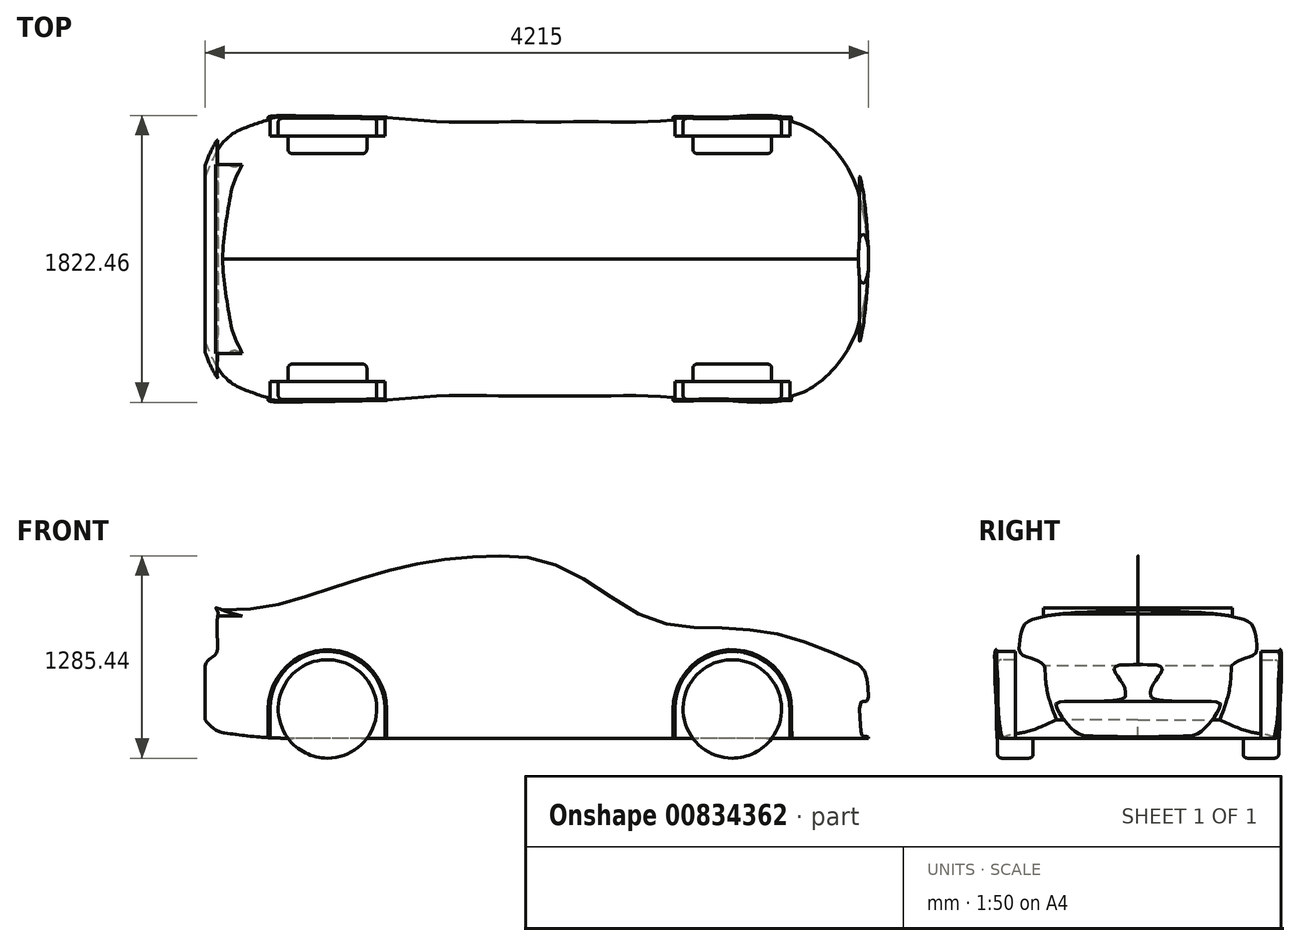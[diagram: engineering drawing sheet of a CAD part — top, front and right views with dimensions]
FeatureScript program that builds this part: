
annotation { "Feature Type Name" : "Feature", "Feature Type Description" : "" }
export const myFeature = defineFeature(function(context is Context, id is Id, definition is map)
    precondition{}
    {
        {
            var Q0;
            Q0=qCreatedBy(makeId("Right.planeOp"),FACE);
            cPlane(context, id + "F0", {"entities" : qUnion([Q0]), "cplaneType" : CPlaneType.OFFSET, "offset" : 400 * mm, "width" : 150 * mm, "height" : 150 * mm});
        }
        {
            var Q0;
            Q0=qCreatedBy(id+"F0.planeOp",FACE);
            cPlane(context, id + "F1", {"entities" : qUnion([Q0]), "cplaneType" : CPlaneType.OFFSET, "offset" : 250 * mm, "width" : 150 * mm, "height" : 150 * mm});
        }
        {
            var Q0;
            Q0=qCreatedBy(id+"F1.planeOp",FACE);
            cPlane(context, id + "F2", {"entities" : qUnion([Q0]), "cplaneType" : CPlaneType.OFFSET, "offset" : 470 * mm, "width" : 150 * mm, "height" : 150 * mm});
        }
        {
            var Q0;
            Q0=qCreatedBy(id+"F2.planeOp",FACE);
            cPlane(context, id + "F3", {"entities" : qUnion([Q0]), "cplaneType" : CPlaneType.OFFSET, "offset" : 390 * mm, "width" : 150 * mm, "height" : 150 * mm});
        }
        {
            var Q0;
            Q0=qCreatedBy(makeId("Right.planeOp"),FACE);
            cPlane(context, id + "F4", {"entities" : qUnion([Q0]), "cplaneType" : CPlaneType.OFFSET, "offset" : 650 * mm, "oppositeDirection" : true, "width" : 150 * mm, "height" : 150 * mm});
        }
        {
            var Q0;
            Q0=qCreatedBy(makeId("Right.planeOp"),FACE);
            cPlane(context, id + "F5", {"entities" : qUnion([Q0]), "cplaneType" : CPlaneType.OFFSET, "offset" : 1080 * mm, "oppositeDirection" : true, "width" : 150 * mm, "height" : 150 * mm});
        }
        {
            var Q0;
            Q0=qCreatedBy(id+"F5.planeOp",FACE);
            cPlane(context, id + "F6", {"entities" : qUnion([Q0]), "cplaneType" : CPlaneType.OFFSET, "offset" : 400 * mm, "oppositeDirection" : true, "width" : 150 * mm, "height" : 150 * mm});
        }
        {
            var Q0;
            Q0=qCreatedBy(id+"F6.planeOp",FACE);
            cPlane(context, id + "F7", {"entities" : qUnion([Q0]), "cplaneType" : CPlaneType.OFFSET, "offset" : 300 * mm, "oppositeDirection" : true, "width" : 150 * mm, "height" : 150 * mm});
        }
        {
            var Q0;
            Q0=qCreatedBy(makeId("Right.planeOp"),FACE);
            var sketch = newSketch(context, id + "F8", { "sketchPlane" : qUnion([Q0])});
            skLineSegment(sketch, "E0", {"start": v(0, 124.5) * mm, "end": v(870, 124.5) * mm});
            skFitSpline(sketch, "E1", {"points": [v(870, 124.5) * mm, v(891.11, 284.5) * mm, v(894.64, 458.04) * mm, v(887.8, 670.78) * mm, v(873.17, 769.8) * mm, v(845.6, 817.1) * mm, v(804.73, 858.33) * mm, v(772.04, 909.97) * mm, v(720.89, 1009.06) * mm, v(649.29, 1152.8) * mm, v(559.76, 1235.3) * mm, v(0, 1252.96) * mm], "startDerivative": vector(362.88, 1642) * mm, "endDerivative": vector(-2009.53, -25.16) * mm});
            skLineSegment(sketch, "E2", {"start": v(0, 0) * mm, "end": v(0, 1252.96) * mm});
            skSolve(sketch);
        }
        {
            var Q0;
            Q0=qCreatedBy(id+"F0.planeOp",FACE);
            var sketch = newSketch(context, id + "F9", { "sketchPlane" : qUnion([Q0])});
            skLineSegment(sketch, "E3", {"start": v(0, 124.5) * mm, "end": v(870, 124.5) * mm});
            skFitSpline(sketch, "E4", {"points": [v(870, 124.5) * mm, v(889.48, 284.5) * mm, v(893.13, 453.1) * mm, v(886.02, 666.74) * mm, v(878.45, 750.6) * mm, v(846.63, 809.81) * mm, v(806.15, 848.41) * mm, v(773.2, 873.84) * mm, v(733.56, 929.45) * mm, v(666.4, 987) * mm, v(525.26, 1024) * mm, v(0, 1039.03) * mm], "startDerivative": vector(258.1, 1763.42) * mm, "endDerivative": vector(-2429.32, 0) * mm});
            skLineSegment(sketch, "E5", {"start": v(0, 124.5) * mm, "end": v(0, 1039.03) * mm});
            skSolve(sketch);
        }
        {
            var Q0;
            Q0=qCreatedBy(id+"F1.planeOp",FACE);
            var sketch = newSketch(context, id + "F10", { "sketchPlane" : qUnion([Q0])});
            skLineSegment(sketch, "E6", {"start": v(0, 124.5) * mm, "end": v(870, 124.5) * mm});
            skFitSpline(sketch, "E7", {"points": [v(870, 124.5) * mm, v(892.1, 284.5) * mm, v(894.52, 460.26) * mm, v(887.06, 674.5) * mm, v(873.24, 753.16) * mm, v(845.97, 795) * mm, v(804.34, 823.62) * mm, v(744.49, 841.84) * mm, v(628.69, 860.05) * mm, v(503.78, 873.07) * mm, v(342.44, 883.47) * mm, v(0, 892.58) * mm], "startDerivative": vector(336.22, 2247.6) * mm, "endDerivative": vector(-2429.27, 12.93) * mm});
            skLineSegment(sketch, "E8", {"start": v(0, 124.5) * mm, "end": v(0, 892.58) * mm});
            skSolve(sketch);
        }
        {
            var Q0;
            Q0=qCreatedBy(id+"F4.planeOp",FACE);
            var sketch = newSketch(context, id + "F11", { "sketchPlane" : qUnion([Q0])});
            skLineSegment(sketch, "E9", {"start": v(0, 124.5) * mm, "end": v(870, 124.5) * mm});
            skFitSpline(sketch, "E10", {"points": [v(870, 124.5) * mm, v(891.22, 284.5) * mm, v(893.85, 457.43) * mm, v(888.43, 668) * mm, v(877.52, 766.78) * mm, v(847.35, 831) * mm, v(806.73, 867.36) * mm, v(772.55, 908.99) * mm, v(713.7, 1043.7) * mm, v(639.2, 1173.93) * mm, v(505.77, 1239) * mm, v(0, 1259.74) * mm], "startDerivative": vector(285.74, 2002.73) * mm, "endDerivative": vector(-2009.53, -25.16) * mm});
            skLineSegment(sketch, "E11", {"start": v(0, 0) * mm, "end": v(0, 1259.74) * mm});
            skSolve(sketch);
        }
        {
            var Q0;
            Q0=qCreatedBy(id+"F5.planeOp",FACE);
            var sketch = newSketch(context, id + "F12", { "sketchPlane" : qUnion([Q0])});
            skLineSegment(sketch, "E12", {"start": v(0, 124.5) * mm, "end": v(901.84, 124.5) * mm});
            skFitSpline(sketch, "E13", {"points": [v(901.84, 124.5) * mm, v(901.84, 445.34) * mm, v(897.17, 659.1) * mm, v(883.08, 776.07) * mm, v(850.9, 838.5) * mm, v(807.82, 870.25) * mm, v(762.15, 901.06) * mm, v(705.47, 979.53) * mm, v(608.15, 1094.45) * mm, v(391.22, 1147.4) * mm, v(0, 1167.07) * mm], "startDerivative": vector(56.05, 2605.66) * mm, "endDerivative": vector(-2009.53, -25.16) * mm});
            skLineSegment(sketch, "E14", {"start": v(0, 0) * mm, "end": v(0, 1167.07) * mm});
            skSolve(sketch);
        }
        {
            var Q0;
            Q0=qCreatedBy(id+"F6.planeOp",FACE);
            var sketch = newSketch(context, id + "F13", { "sketchPlane" : qUnion([Q0])});
            skLineSegment(sketch, "E15", {"start": v(0, 124.5) * mm, "end": v(905.35, 124.5) * mm});
            skFitSpline(sketch, "E16", {"points": [v(905.35, 124.5) * mm, v(911.49, 507.78) * mm, v(901.23, 717.66) * mm, v(864.15, 828.08) * mm, v(805.53, 864.3) * mm, v(709.87, 894.97) * mm, v(662.3, 933.8) * mm, v(611.81, 968.75) * mm, v(468.12, 1007.59) * mm, v(200.58, 1032.29) * mm, v(0, 1036.7) * mm], "startDerivative": vector(35.6, 1166.72) * mm, "endDerivative": vector(-2009.53, -25.16) * mm});
            skLineSegment(sketch, "E17", {"start": v(0, 100.04) * mm, "end": v(0, 1036.7) * mm});
            skSolve(sketch);
        }
        {
            var Q0;
            Q0=qCreatedBy(id+"F2.planeOp",FACE);
            var sketch = newSketch(context, id + "F14", { "sketchPlane" : qUnion([Q0])});
            skLineSegment(sketch, "E18", {"start": v(0, 124.5) * mm, "end": v(903.74, 124.5) * mm});
            skFitSpline(sketch, "E19", {"points": [v(903.74, 124.5) * mm, v(916.37, 455.49) * mm, v(900.5, 679.08) * mm, v(857.9, 771.6) * mm, v(782.93, 814.08) * mm, v(692.41, 799.23) * mm, v(637.01, 783.4) * mm, v(575.02, 780.76) * mm, v(449.7, 795.27) * mm, v(267.68, 816.38) * mm, v(0, 826.93) * mm], "startDerivative": vector(154.78, 2385.54) * mm, "endDerivative": vector(-2429.32, -1.4) * mm});
            skLineSegment(sketch, "E20", {"start": v(0, 124.5) * mm, "end": v(0, 826.93) * mm});
            skSolve(sketch);
        }
        {
            var Q0;
            Q0=qCreatedBy(id+"F3.planeOp",FACE);
            var sketch = newSketch(context, id + "F15", { "sketchPlane" : qUnion([Q0])});
            skLineSegment(sketch, "E21", {"start": v(0, 124.5) * mm, "end": v(885.85, 124.5) * mm});
            skFitSpline(sketch, "E22", {"points": [v(885.85, 124.5) * mm, v(903.62, 270.39) * mm, v(904.2, 467.45) * mm, v(859.81, 719.76) * mm, v(768.6, 771) * mm, v(666.13, 754.75) * mm, v(542.72, 724.7) * mm, v(464.05, 723.61) * mm, v(376.77, 736.54) * mm, v(261.46, 760.25) * mm, v(152.62, 774.26) * mm, v(0, 781.8) * mm], "startDerivative": vector(300.47, 1117.8) * mm, "endDerivative": vector(-2429.32, -1.4) * mm});
            skLineSegment(sketch, "E23", {"start": v(0, 124.5) * mm, "end": v(0, 781.8) * mm});
            skSolve(sketch);
        }
        {
            var Q0;
            Q0=qCreatedBy(id+"F3.planeOp",FACE);
            cPlane(context, id + "F16", {"entities" : qUnion([Q0]), "cplaneType" : CPlaneType.OFFSET, "offset" : 300 * mm, "width" : 150 * mm, "height" : 150 * mm});
        }
        {
            var Q0;
            Q0=qCreatedBy(id+"F16.planeOp",FACE);
            var sketch = newSketch(context, id + "F17", { "sketchPlane" : qUnion([Q0])});
            skLineSegment(sketch, "E24", {"start": v(0, 124.5) * mm, "end": v(728.16, 124.5) * mm});
            skFitSpline(sketch, "E25", {"points": [v(728.16, 124.5) * mm, v(790.88, 438.77) * mm, v(756.31, 575.08) * mm, v(668.27, 639.2) * mm, v(496.33, 652.7) * mm, v(405.95, 657.45) * mm, v(317.95, 663.4) * mm, v(215.67, 669.34) * mm, v(121.8, 673) * mm, v(0, 677.25) * mm], "startDerivative": vector(683.35, 2007.11) * mm, "endDerivative": vector(-1315.52, 16.5) * mm});
            skLineSegment(sketch, "E26", {"start": v(0, 124.5) * mm, "end": v(0, 677.25) * mm});
            skSolve(sketch);
        }
        {
            var Q0;
            Q0=qCreatedBy(id+"F16.planeOp",FACE);
            cPlane(context, id + "F18", {"entities" : qUnion([Q0]), "cplaneType" : CPlaneType.OFFSET, "offset" : 175 * mm, "width" : 150 * mm, "height" : 150 * mm});
        }
        {
            var Q0;
            Q0=qCreatedBy(id+"F18.planeOp",FACE);
            var sketch = newSketch(context, id + "F19", { "sketchPlane" : qUnion([Q0])});
            skLineSegment(sketch, "E27", {"start": v(0, 124.5) * mm, "end": v(450, 124.5) * mm});
            skFitSpline(sketch, "E28", {"points": [v(450, 124.5) * mm, v(487.77, 181.4) * mm, v(571.26, 329.58) * mm, v(600.39, 467.6) * mm, v(581.4, 527.1) * mm, v(497.82, 563.83) * mm, v(383.86, 580.3) * mm, v(269.9, 592.95) * mm, v(152.4, 598.78) * mm, v(0, 600) * mm], "startDerivative": vector(794.98, 1097.59) * mm, "endDerivative": vector(-2440.18, 24.53) * mm});
            skLineSegment(sketch, "E29", {"start": v(0, 124.5) * mm, "end": v(0, 600) * mm});
            skSolve(sketch);
        }
        {
            var Q0;
            Q0=qCreatedBy(id+"F18.planeOp",FACE);
            cPlane(context, id + "F20", {"entities" : qUnion([Q0]), "cplaneType" : CPlaneType.OFFSET, "offset" : 75 * mm, "width" : 150 * mm, "height" : 150 * mm});
        }
        {
            var Q0;
            Q0=qCreatedBy(id+"F20.planeOp",FACE);
            var sketch = newSketch(context, id + "F21", { "sketchPlane" : qUnion([Q0])});
            skLineSegment(sketch, "E30", {"start": v(0, 124.5) * mm, "end": v(20.31, 124.5) * mm});
            skFitSpline(sketch, "E31", {"points": [v(20.31, 124.5) * mm, v(48.12, 155) * mm, v(57.63, 231.82) * mm, v(57.08, 273.61) * mm, v(38.48, 458.21) * mm, v(16.04, 541.01) * mm, v(0, 565.46) * mm], "startDerivative": vector(421.48, 102.59) * mm, "endDerivative": vector(-203.78, 250.22) * mm});
            skLineSegment(sketch, "E32", {"start": v(0, 124.5) * mm, "end": v(0, 565.46) * mm});
            skSolve(sketch);
        }
        {
            var Q0;
            Q0=qCreatedBy(id+"F7.planeOp",FACE);
            var sketch = newSketch(context, id + "F22", { "sketchPlane" : qUnion([Q0])});
            skLineSegment(sketch, "E33", {"start": v(0, 131.73) * mm, "end": v(875, 131.73) * mm});
            skFitSpline(sketch, "E34", {"points": [v(875, 131.73) * mm, v(895.55, 627.68) * mm, v(848.53, 820.84) * mm, v(812.95, 851.34) * mm, v(754.12, 880.67) * mm, v(696.63, 896.7) * mm, v(604.5, 918.2) * mm, v(498.32, 932.44) * mm, v(350.54, 945.58) * mm, v(198.38, 953.24) * mm, v(0, 958.71) * mm], "startDerivative": vector(247.43, 1101.88) * mm, "endDerivative": vector(-2009.53, -25.16) * mm});
            skLineSegment(sketch, "E35", {"start": v(0, 131.73) * mm, "end": v(0, 958.71) * mm});
            skSolve(sketch);
        }
        {
            var Q0;
            Q0=qCreatedBy(id+"F7.planeOp",FACE);
            cPlane(context, id + "F23", {"entities" : qUnion([Q0]), "cplaneType" : CPlaneType.OFFSET, "offset" : 100 * mm, "oppositeDirection" : true, "width" : 150 * mm, "height" : 150 * mm});
        }
        {
            var Q0;
            Q0=qCreatedBy(id+"F23.planeOp",FACE);
            var sketch = newSketch(context, id + "F24", { "sketchPlane" : qUnion([Q0])});
            skLineSegment(sketch, "E36", {"start": v(0, 140.57) * mm, "end": v(840.25, 140.57) * mm});
            skFitSpline(sketch, "E37", {"points": [v(840.25, 140.57) * mm, v(875.51, 631.89) * mm, v(816.68, 820.6) * mm, v(761.84, 865.46) * mm, v(730.93, 879.42) * mm, v(659.57, 898.6) * mm, v(504.06, 921.3) * mm, v(347.08, 933.67) * mm, v(195.8, 942.23) * mm, v(0, 947.94) * mm], "startDerivative": vector(247.43, 1101.88) * mm, "endDerivative": vector(-2009.53, -25.16) * mm});
            skLineSegment(sketch, "E38", {"start": v(0, 140.57) * mm, "end": v(0, 947.94) * mm});
            skSolve(sketch);
        }
        {
            var Q0;
            Q0=qCreatedBy(id+"F23.planeOp",FACE);
            cPlane(context, id + "F25", {"entities" : qUnion([Q0]), "cplaneType" : CPlaneType.OFFSET, "offset" : 100 * mm, "oppositeDirection" : true, "width" : 150 * mm, "height" : 150 * mm});
        }
        {
            var Q0;
            Q0=qCreatedBy(id+"F25.planeOp",FACE);
            var sketch = newSketch(context, id + "F26", { "sketchPlane" : qUnion([Q0])});
            skLineSegment(sketch, "E39", {"start": v(0, 153.5) * mm, "end": v(793.13, 153.5) * mm});
            skFitSpline(sketch, "E40", {"points": [v(793.13, 153.5) * mm, v(840.94, 565.1) * mm, v(819.62, 753.63) * mm, v(783.5, 825.87) * mm, v(727.03, 868.6) * mm, v(615.36, 896.75) * mm, v(494.35, 916.17) * mm, v(345.22, 927.13) * mm, v(195.18, 935.34) * mm, v(0, 942.06) * mm], "startDerivative": vector(247.43, 1101.88) * mm, "endDerivative": vector(-2152.48, 17.87) * mm});
            skLineSegment(sketch, "E41", {"start": v(0, 153.5) * mm, "end": v(0, 942.06) * mm});
            skSolve(sketch);
        }
        {
            var Q0;
            Q0=qCreatedBy(id+"F25.planeOp",FACE);
            cPlane(context, id + "F27", {"entities" : qUnion([Q0]), "cplaneType" : CPlaneType.OFFSET, "offset" : 100 * mm, "oppositeDirection" : true, "width" : 150 * mm, "height" : 150 * mm});
        }
        {
            var Q0;
            Q0=qCreatedBy(id+"F27.planeOp",FACE);
            var sketch = newSketch(context, id + "F28", { "sketchPlane" : qUnion([Q0])});
            skLineSegment(sketch, "E42", {"start": v(0, 174.6) * mm, "end": v(683.45, 174.6) * mm});
            skFitSpline(sketch, "E43", {"points": [v(683.45, 174.6) * mm, v(735.3, 492.43) * mm, v(749.1, 628.88) * mm, v(750.05, 710.3) * mm, v(742.83, 783.93) * mm, v(712.34, 855.59) * mm, v(533.98, 907.4) * mm, v(348.57, 924.53) * mm, v(193.74, 932.96) * mm, v(0, 938) * mm], "startDerivative": vector(247.43, 1101.88) * mm, "endDerivative": vector(-2009.53, -25.16) * mm});
            skLineSegment(sketch, "E44", {"start": v(0, 174.6) * mm, "end": v(0, 938) * mm});
            skSolve(sketch);
        }
        {
            var Q0;
            Q0=qCreatedBy(id+"F27.planeOp",FACE);
            cPlane(context, id + "F29", {"entities" : qUnion([Q0]), "cplaneType" : CPlaneType.OFFSET, "offset" : 75 * mm, "oppositeDirection" : true, "width" : 150 * mm, "height" : 150 * mm});
        }
        {
            var Q0;
            Q0=qCreatedBy(id+"F29.planeOp",FACE);
            var sketch = newSketch(context, id + "F30", { "sketchPlane" : qUnion([Q0])});
            skLineSegment(sketch, "E45", {"start": v(0, 243.7) * mm, "end": v(518.67, 243.7) * mm});
            skFitSpline(sketch, "E46", {"points": [v(518.67, 243.7) * mm, v(555.55, 342.69) * mm, v(573.99, 407.71) * mm, v(585.82, 481.34) * mm, v(593.78, 588.71) * mm, v(596.34, 683.74) * mm, v(568.3, 813.43) * mm, v(436.27, 885.87) * mm, v(200.09, 918.78) * mm, v(0, 925.4) * mm], "startDerivative": vector(819.23, 2090.44) * mm, "endDerivative": vector(-2009.53, -25.16) * mm});
            skLineSegment(sketch, "E47", {"start": v(0, 243.7) * mm, "end": v(0, 925.4) * mm});
            skSolve(sketch);
        }
        {
            var Q0;
            Q0=qCreatedBy(makeId("Right.planeOp"),FACE);
            cPlane(context, id + "F31", {"entities" : qUnion([Q0]), "cplaneType" : CPlaneType.OFFSET, "offset" : 300 * mm, "oppositeDirection" : true, "width" : 150 * mm, "height" : 150 * mm});
        }
        {
            var Q0;
            Q0=qCreatedBy(id+"F31.planeOp",FACE);
            var sketch = newSketch(context, id + "F32", { "sketchPlane" : qUnion([Q0])});
            skLineSegment(sketch, "E48", {"start": v(0, 124.5) * mm, "end": v(870, 124.5) * mm});
            skFitSpline(sketch, "E49", {"points": [v(870, 124.5) * mm, v(890.9, 284.5) * mm, v(895.01, 459.58) * mm, v(889.19, 670.45) * mm, v(873.39, 770.2) * mm, v(847.02, 819.24) * mm, v(805.69, 861.82) * mm, v(772.37, 914.43) * mm, v(739.95, 995.86) * mm, v(646.01, 1201.01) * mm, v(518.28, 1262.42) * mm, v(0, 1285) * mm], "startDerivative": vector(400.8, 1802.26) * mm, "endDerivative": vector(-2009.53, -25.16) * mm});
            skLineSegment(sketch, "E50", {"start": v(0, 0) * mm, "end": v(0, 1285) * mm});
            skSolve(sketch);
        }
        {
            var Q0;
            Q0=makeQuery(id+"F21.imprint","IMPRINT",FACE,{"disambiguationData":[TD([[makeQuery(id+"F21.imprint","IMPRINT",EDGE,{"derivedFrom":sQuery(id+"F21.wireOp",EDGE,"E30")}),1.0]])]});
            var Q1;
            Q1=makeQuery(id+"F19.imprint","IMPRINT",FACE,{"disambiguationData":[TD([[makeQuery(id+"F19.imprint","IMPRINT",EDGE,{"derivedFrom":sQuery(id+"F19.wireOp",EDGE,"E27")}),1.0]])]});
            var Q2;
            Q2=makeQuery(id+"F17.imprint","IMPRINT",FACE,{"disambiguationData":[TD([[makeQuery(id+"F17.imprint","IMPRINT",EDGE,{"derivedFrom":sQuery(id+"F17.wireOp",EDGE,"E24")}),1.0]])]});
            var Q3;
            Q3=makeQuery(id+"F15.imprint","IMPRINT",FACE,{"disambiguationData":[TD([[makeQuery(id+"F15.imprint","IMPRINT",EDGE,{"derivedFrom":sQuery(id+"F15.wireOp",EDGE,"E21")}),1.0]])]});
            var Q4;
            Q4=makeQuery(id+"F14.imprint","IMPRINT",FACE,{"disambiguationData":[TD([[makeQuery(id+"F14.imprint","IMPRINT",EDGE,{"derivedFrom":sQuery(id+"F14.wireOp",EDGE,"E18")}),1.0]])]});
            var Q5;
            Q5=makeQuery(id+"F10.imprint","IMPRINT",FACE,{"disambiguationData":[TD([[makeQuery(id+"F10.imprint","IMPRINT",EDGE,{"derivedFrom":sQuery(id+"F10.wireOp",EDGE,"E6")}),1.0]])]});
            var Q6;
            Q6=makeQuery(id+"F9.imprint","IMPRINT",FACE,{"disambiguationData":[TD([[makeQuery(id+"F9.imprint","IMPRINT",EDGE,{"derivedFrom":sQuery(id+"F9.wireOp",EDGE,"E3")}),1.0]])]});
            var Q7;
            {var subQ0=sQuery(id+"F8.wireOp",EDGE,"E0");Q7=makeQuery(id+"F8.imprint","IMPRINT",FACE,{"disambiguationData":[TD([[makeQuery(id+"F8.imprint","IMPRINT",EDGE,{"derivedFrom":subQ0}),1.0]])]});}
            var Q8;
            {var subQ0=sQuery(id+"F32.wireOp",EDGE,"E48");Q8=makeQuery(id+"F32.imprint","IMPRINT",FACE,{"disambiguationData":[TD([[makeQuery(id+"F32.imprint","IMPRINT",EDGE,{"derivedFrom":subQ0}),1.0]])]});}
            var Q9;
            {var subQ0=sQuery(id+"F11.wireOp",EDGE,"E9");Q9=makeQuery(id+"F11.imprint","IMPRINT",FACE,{"disambiguationData":[TD([[makeQuery(id+"F11.imprint","IMPRINT",EDGE,{"derivedFrom":subQ0}),1.0]])]});}
            var Q10;
            {var subQ0=sQuery(id+"F12.wireOp",EDGE,"E12");Q10=makeQuery(id+"F12.imprint","IMPRINT",FACE,{"disambiguationData":[TD([[makeQuery(id+"F12.imprint","IMPRINT",EDGE,{"derivedFrom":subQ0}),1.0]])]});}
            var Q11;
            {var subQ0=sQuery(id+"F13.wireOp",EDGE,"E15");Q11=makeQuery(id+"F13.imprint","IMPRINT",FACE,{"disambiguationData":[TD([[makeQuery(id+"F13.imprint","IMPRINT",EDGE,{"derivedFrom":subQ0}),1.0]])]});}
            var Q12;
            Q12=makeQuery(id+"F22.imprint","IMPRINT",FACE,{"disambiguationData":[TD([[makeQuery(id+"F22.imprint","IMPRINT",EDGE,{"derivedFrom":sQuery(id+"F22.wireOp",EDGE,"E33")}),1.0]])]});
            var Q13;
            Q13=makeQuery(id+"F24.imprint","IMPRINT",FACE,{"disambiguationData":[TD([[makeQuery(id+"F24.imprint","IMPRINT",EDGE,{"derivedFrom":sQuery(id+"F24.wireOp",EDGE,"E36")}),1.0]])]});
            var Q14;
            Q14=makeQuery(id+"F26.imprint","IMPRINT",FACE,{"disambiguationData":[TD([[makeQuery(id+"F26.imprint","IMPRINT",EDGE,{"derivedFrom":sQuery(id+"F26.wireOp",EDGE,"E39")}),1.0]])]});
            var Q15;
            Q15=makeQuery(id+"F28.imprint","IMPRINT",FACE,{"disambiguationData":[TD([[makeQuery(id+"F28.imprint","IMPRINT",EDGE,{"derivedFrom":sQuery(id+"F28.wireOp",EDGE,"E42")}),1.0]])]});
            var Q16;
            Q16=makeQuery(id+"F30.imprint","IMPRINT",FACE,{"disambiguationData":[TD([[makeQuery(id+"F30.imprint","IMPRINT",EDGE,{"derivedFrom":sQuery(id+"F30.wireOp",EDGE,"E45")}),1.0]])]});
            loft(context, id + "F33", {"sheetProfilesArray" : [{ "sheetProfileEntities" : qUnion([Q0]) }, { "sheetProfileEntities" : qUnion([Q1]) }, { "sheetProfileEntities" : qUnion([Q2]) }, { "sheetProfileEntities" : qUnion([Q3]) }, { "sheetProfileEntities" : qUnion([Q4]) }, { "sheetProfileEntities" : qUnion([Q5]) }, { "sheetProfileEntities" : qUnion([Q6]) }, { "sheetProfileEntities" : qUnion([Q7]) }, { "sheetProfileEntities" : qUnion([Q8]) }, { "sheetProfileEntities" : qUnion([Q9]) }, { "sheetProfileEntities" : qUnion([Q10]) }, { "sheetProfileEntities" : qUnion([Q11]) }, { "sheetProfileEntities" : qUnion([Q12]) }, { "sheetProfileEntities" : qUnion([Q13]) }, { "sheetProfileEntities" : qUnion([Q14]) }, { "sheetProfileEntities" : qUnion([Q15]) }, { "sheetProfileEntities" : qUnion([Q16]) }]});
        }
        {
            var Q0;
            Q0=qCreatedBy(makeId("Front.planeOp"),FACE);
            var sketch = newSketch(context, id + "F34", { "sketchPlane" : qUnion([Q0])});
            skFitSpline(sketch, "E51", {"points": [v(-1917.38, 979.85) * mm, v(-1956.53, 970.24) * mm, v(-2006.78, 944.86) * mm, v(-2067.13, 924.34) * mm, v(-2076.98, 685.24) * mm, v(-2100.65, 648.2) * mm, v(-2150.92, 598.3) * mm, v(-2175.98, 516.12) * mm], "startDerivative": vector(-1093.34, 0) * mm, "endDerivative": vector(-364.89, -456.13) * mm});
            skLineSegment(sketch, "E52", {"start": v(-1917.38, 979.85) * mm, "end": v(-2175.98, 979.85) * mm});
            skLineSegment(sketch, "E53", {"start": v(-2175.98, 979.85) * mm, "end": v(-2175.98, 516.12) * mm});
            skSolve(sketch);
        }
        {
            var Q0;
            Q0=qSketchRegion(id+"F34",true);
            extrude(context, id + "F35", {"entities" : qUnion([Q0]), "operationType" : NewBodyOperationType.REMOVE, "endBound" : BoundingType.THROUGH_ALL, "oppositeDirection" : true, "depth" : 25 * mm, "offsetDistance" : 25 * mm});
        }
        {
            var Q0;
            Q0=qCreatedBy(makeId("Front.planeOp"),FACE);
            var sketch = newSketch(context, id + "F36", { "sketchPlane" : qUnion([Q0])});
            skFitSpline(sketch, "E54", {"points": [v(1972.46, 610.84) * mm, v(2031.27, 555.02) * mm, v(2055.59, 437.45) * mm, v(2056.54, 416.38) * mm, v(2050.67, 365.07) * mm, v(2023.54, 360.1) * mm, v(2007.36, 352.64) * mm, v(2002.8, 328.47) * mm, v(2012.88, 156.12) * mm, v(2022.53, 141.85) * mm, v(2042.14, 137.47) * mm, v(2070.66, 135.45) * mm], "startDerivative": vector(440.78, -315.33) * mm, "endDerivative": vector(389.64, -13) * mm});
            skLineSegment(sketch, "E55", {"start": v(1972.46, 610.84) * mm, "end": v(2072.53, 610.84) * mm});
            skLineSegment(sketch, "E56", {"start": v(2072.53, 610.84) * mm, "end": v(2070.66, 135.45) * mm});
            skSolve(sketch);
        }
        {
            var Q0;
            Q0=qSketchRegion(id+"F36",true);
            extrude(context, id + "F37", {"entities" : qUnion([Q0]), "operationType" : NewBodyOperationType.REMOVE, "endBound" : BoundingType.THROUGH_ALL, "oppositeDirection" : true, "depth" : 25 * mm, "offsetDistance" : 25 * mm});
        }
        {
            var Q0;
            Q0=qCreatedBy(makeId("Front.planeOp"),FACE);
            cPlane(context, id + "F38", {"entities" : qUnion([Q0]), "cplaneType" : CPlaneType.OFFSET, "offset" : 780 * mm, "oppositeDirection" : true, "width" : 150 * mm, "height" : 150 * mm});
        }
        {
            var Q0;
            Q0=qCreatedBy(id+"F38.planeOp",FACE);
            var sketch = newSketch(context, id + "F39", { "sketchPlane" : qUnion([Q0])});
            skLineSegment(sketch, "E57", {"start": v(0, 0) * mm, "end": v(1670.97, 0) * mm});
            skLineSegment(sketch, "E58", {"start": v(0, 0) * mm, "end": v(-1932.5, 0) * mm});
            skCircle(sketch, "E59", {"center": v(1193.68, 312.75) * mm, "radius": 312.75 * mm});
            skCircle(sketch, "E60", {"center": v(-1377.32, 312.75) * mm, "radius": 312.75 * mm});
            skSolve(sketch);
        }
        {
            var Q0;
            Q0=qCreatedBy(makeId("Front.planeOp"),FACE);
            var sketch = newSketch(context, id + "F40", { "sketchPlane" : qUnion([Q0])});
            skFitSpline(sketch, "E61", {"points": [v(-1978.2, 887.35) * mm, v(-2038.48, 935.18) * mm, v(-2075.08, 970.35) * mm, v(-2098.48, 1000.33) * mm, v(-2113.84, 1021.9) * mm, v(-2121.07, 1026) * mm, v(-2122.59, 1021.36) * mm, v(-2102.8, 983.86) * mm, v(-2079.36, 938.58) * mm, v(-2066.67, 895.03) * mm], "startDerivative": vector(-303.48, 195.1) * mm, "endDerivative": vector(40.4, -387.87) * mm});
            skLineSegment(sketch, "E62", {"start": v(-1978.2, 887.35) * mm, "end": v(-2066.67, 895.03) * mm});
            skSolve(sketch);
        }
        {
            var Q0;
            Q0=qCreatedBy(id+"F38.planeOp",FACE);
            var sketch = newSketch(context, id + "F41", { "sketchPlane" : qUnion([Q0])});
            skArc(sketch, "E63", {"start": v(1558.68, 312.75) * mm, "mid": v(1193.68, 677.75) * mm, "end": v(828.68, 312.75) * mm});
            skArc(sketch, "E64", {"start": v(-1012.32, 312.75) * mm, "mid": v(-1377.32, 677.75) * mm, "end": v(-1742.32, 312.75) * mm});
            skLineSegment(sketch, "E65", {"start": v(1558.68, 312.75) * mm, "end": v(1558.68, -81.3) * mm});
            skLineSegment(sketch, "E66", {"start": v(828.68, 312.75) * mm, "end": v(828.68, -81.3) * mm});
            skLineSegment(sketch, "E67", {"start": v(828.68, -81.3) * mm, "end": v(1558.68, -81.3) * mm});
            skLineSegment(sketch, "E68", {"start": v(-1012.32, 312.75) * mm, "end": v(-1012.32, -110.96) * mm});
            skLineSegment(sketch, "E69", {"start": v(-1742.32, 312.75) * mm, "end": v(-1742.32, -110.96) * mm});
            skLineSegment(sketch, "E70", {"start": v(-1742.32, -110.96) * mm, "end": v(-1012.32, -110.96) * mm});
            skSolve(sketch);
        }
        {
            var Q0;
            Q0 = qSketchRegion(id + "F41", true);
            extrude(context, id + "F42", {"entities" : qUnion([Q0]), "operationType" : NewBodyOperationType.REMOVE, "endBound" : BoundingType.THROUGH_ALL, "oppositeDirection" : true, "depth" : 25 * mm, "offsetDistance" : 25 * mm});
        }
        {
            var Q0;
            Q0=makeQuery(id+"F39.imprint","IMPRINT",FACE,{"disambiguationData":[TD([[makeQuery(id+"F39.imprint","IMPRINT",EDGE,{"derivedFrom":sQuery(id+"F39.wireOp",EDGE,"E59")}),1.0]])]});
            var Q1;
            Q1=makeQuery(id+"F39.imprint","IMPRINT",FACE,{"disambiguationData":[TD([[makeQuery(id+"F39.imprint","IMPRINT",EDGE,{"derivedFrom":sQuery(id+"F39.wireOp",EDGE,"E60")}),1.0]])]});
            extrude(context, id + "F43", {"entities" : qUnion([Q0, Q1]), "operationType" : NewBodyOperationType.ADD, "depth" : 225 * mm, "offsetDistance" : 25 * mm, "symmetric" : true});
        }
        {
            var Q0;
            Q0=makeQuery(id+"F43.opExtrude","CAP_EDGE",EDGE,{"disambiguationData":[OSD([sQuery(id+"F39.wireOp",EDGE,"E59")])],"isStart":false});
            var Q1;
            Q1=makeQuery(id+"F43.opExtrude","CAP_EDGE",EDGE,{"disambiguationData":[OSD([sQuery(id+"F39.wireOp",EDGE,"E59")])],"isStart":true});
            var Q2;
            Q2=makeQuery(id+"F43.opExtrude","CAP_EDGE",EDGE,{"disambiguationData":[OSD([sQuery(id+"F39.wireOp",EDGE,"E60")])],"isStart":false});
            var Q3;
            Q3=makeQuery(id+"F43.opExtrude","CAP_EDGE",EDGE,{"disambiguationData":[OSD([sQuery(id+"F39.wireOp",EDGE,"E60")])],"isStart":true});
            fillet(context, id + "F44", {"entities" : qUnion([Q0, Q1, Q2, Q3]), "radius" : 25 * mm, "tangentPropagation" : true, "allowEdgeOverflow" : false});
        }
        {
            var Q0;
            {var subQ0=sQuery(id+"F32.wireOp",EDGE,"E49");var subQ1=sQuery(id+"F32.wireOp",EDGE,"E50");var subQ2=sQuery(id+"F32.wireOp",EDGE,"E48");var subQ3=sQuery(id+"F30.wireOp",EDGE,"E46");var subQ4=sQuery(id+"F30.wireOp",EDGE,"E47");var subQ5=sQuery(id+"F30.wireOp",EDGE,"E45");var subQ6=sQuery(id+"F28.wireOp",EDGE,"E43");var subQ7=sQuery(id+"F28.wireOp",EDGE,"E44");var subQ8=sQuery(id+"F28.wireOp",EDGE,"E42");var subQ9=sQuery(id+"F26.wireOp",EDGE,"E40");var subQ10=sQuery(id+"F26.wireOp",EDGE,"E41");var subQ11=sQuery(id+"F26.wireOp",EDGE,"E39");var subQ12=sQuery(id+"F24.wireOp",EDGE,"E37");var subQ13=sQuery(id+"F24.wireOp",EDGE,"E38");var subQ14=sQuery(id+"F24.wireOp",EDGE,"E36");var subQ15=sQuery(id+"F22.wireOp",EDGE,"E34");var subQ16=sQuery(id+"F22.wireOp",EDGE,"E35");var subQ17=sQuery(id+"F22.wireOp",EDGE,"E33");var subQ18=sQuery(id+"F21.wireOp",EDGE,"E31");var subQ19=sQuery(id+"F21.wireOp",EDGE,"E32");var subQ20=sQuery(id+"F21.wireOp",EDGE,"E30");var subQ21=sQuery(id+"F19.wireOp",EDGE,"E28");var subQ22=sQuery(id+"F19.wireOp",EDGE,"E29");var subQ23=sQuery(id+"F19.wireOp",EDGE,"E27");var subQ24=sQuery(id+"F17.wireOp",EDGE,"E25");var subQ25=sQuery(id+"F17.wireOp",EDGE,"E26");var subQ26=sQuery(id+"F17.wireOp",EDGE,"E24");var subQ27=sQuery(id+"F15.wireOp",EDGE,"E22");var subQ28=sQuery(id+"F15.wireOp",EDGE,"E23");var subQ29=sQuery(id+"F15.wireOp",EDGE,"E21");var subQ30=sQuery(id+"F14.wireOp",EDGE,"E19");var subQ31=sQuery(id+"F14.wireOp",EDGE,"E20");var subQ32=sQuery(id+"F14.wireOp",EDGE,"E18");var subQ33=sQuery(id+"F13.wireOp",EDGE,"E16");var subQ34=sQuery(id+"F13.wireOp",EDGE,"E17");var subQ35=sQuery(id+"F13.wireOp",EDGE,"E15");var subQ36=sQuery(id+"F12.wireOp",EDGE,"E13");var subQ37=sQuery(id+"F12.wireOp",EDGE,"E14");var subQ38=sQuery(id+"F12.wireOp",EDGE,"E12");var subQ39=sQuery(id+"F11.wireOp",EDGE,"E10");var subQ40=sQuery(id+"F11.wireOp",EDGE,"E11");var subQ41=sQuery(id+"F11.wireOp",EDGE,"E9");var subQ42=sQuery(id+"F10.wireOp",EDGE,"E7");var subQ43=sQuery(id+"F10.wireOp",EDGE,"E8");var subQ44=sQuery(id+"F10.wireOp",EDGE,"E6");var subQ45=sQuery(id+"F9.wireOp",EDGE,"E4");var subQ46=sQuery(id+"F9.wireOp",EDGE,"E5");var subQ47=sQuery(id+"F9.wireOp",EDGE,"E3");var subQ48=sQuery(id+"F8.wireOp",EDGE,"E1");var subQ49=sQuery(id+"F8.wireOp",EDGE,"E2");var subQ50=sQuery(id+"F8.wireOp",EDGE,"E0");Q0=makeQuery(id+"F42.boolean.opBoolean","INTERSECT",EDGE,{"derivedFrom":[makeQuery(id+"F33.opLoft","SWEPT_FACE",FACE,{"disambiguationData":[OSD([subQ50,subQ48,subQ49,subQ47,subQ45,subQ46,subQ44,subQ42,subQ43,subQ41,subQ39,subQ40,subQ38,subQ36,subQ37,subQ35,subQ33,subQ34,subQ32,subQ30,subQ31,subQ29,subQ27,subQ28,subQ26,subQ24,subQ25,subQ23,subQ21,subQ22,subQ20,subQ18,subQ19,subQ17,subQ15,subQ16,subQ14,subQ12,subQ13,subQ11,subQ9,subQ10,subQ8,subQ6,subQ7,subQ5,subQ3,subQ4,subQ2,subQ0,subQ1]),TDD([makeQuery(id+"F8.imprint","INTERSECT",VERTEX,{"derivedFrom":[subQ50,subQ48]}),makeQuery(id+"F8.imprint","INTERSECT",VERTEX,{"derivedFrom":[subQ48,subQ49]}),makeQuery(id+"F8.imprint","IMPRINT",EDGE,{"derivedFrom":subQ48}),makeQuery(id+"F9.imprint","INTERSECT",VERTEX,{"derivedFrom":[subQ47,subQ45]}),makeQuery(id+"F9.imprint","INTERSECT",VERTEX,{"derivedFrom":[subQ45,subQ46]}),makeQuery(id+"F9.imprint","IMPRINT",EDGE,{"derivedFrom":subQ45}),makeQuery(id+"F10.imprint","INTERSECT",VERTEX,{"derivedFrom":[subQ44,subQ42]}),makeQuery(id+"F10.imprint","INTERSECT",VERTEX,{"derivedFrom":[subQ42,subQ43]}),makeQuery(id+"F10.imprint","IMPRINT",EDGE,{"derivedFrom":subQ42}),makeQuery(id+"F11.imprint","INTERSECT",VERTEX,{"derivedFrom":[subQ41,subQ39]}),makeQuery(id+"F11.imprint","INTERSECT",VERTEX,{"derivedFrom":[subQ39,subQ40]}),makeQuery(id+"F11.imprint","IMPRINT",EDGE,{"derivedFrom":subQ39}),makeQuery(id+"F12.imprint","INTERSECT",VERTEX,{"derivedFrom":[subQ38,subQ36]}),makeQuery(id+"F12.imprint","INTERSECT",VERTEX,{"derivedFrom":[subQ36,subQ37]}),makeQuery(id+"F12.imprint","IMPRINT",EDGE,{"derivedFrom":subQ36}),makeQuery(id+"F13.imprint","INTERSECT",VERTEX,{"derivedFrom":[subQ35,subQ33]}),makeQuery(id+"F13.imprint","INTERSECT",VERTEX,{"derivedFrom":[subQ33,subQ34]}),makeQuery(id+"F13.imprint","IMPRINT",EDGE,{"derivedFrom":subQ33}),makeQuery(id+"F14.imprint","INTERSECT",VERTEX,{"derivedFrom":[subQ32,subQ30]}),makeQuery(id+"F14.imprint","INTERSECT",VERTEX,{"derivedFrom":[subQ30,subQ31]}),makeQuery(id+"F14.imprint","IMPRINT",EDGE,{"derivedFrom":subQ30}),makeQuery(id+"F15.imprint","INTERSECT",VERTEX,{"derivedFrom":[subQ29,subQ27]}),makeQuery(id+"F15.imprint","INTERSECT",VERTEX,{"derivedFrom":[subQ27,subQ28]}),makeQuery(id+"F15.imprint","IMPRINT",EDGE,{"derivedFrom":subQ27}),makeQuery(id+"F17.imprint","INTERSECT",VERTEX,{"derivedFrom":[subQ26,subQ24]}),makeQuery(id+"F17.imprint","INTERSECT",VERTEX,{"derivedFrom":[subQ24,subQ25]}),makeQuery(id+"F17.imprint","IMPRINT",EDGE,{"derivedFrom":subQ24}),makeQuery(id+"F19.imprint","INTERSECT",VERTEX,{"derivedFrom":[subQ23,subQ21]}),makeQuery(id+"F19.imprint","INTERSECT",VERTEX,{"derivedFrom":[subQ21,subQ22]}),makeQuery(id+"F19.imprint","IMPRINT",EDGE,{"derivedFrom":subQ21}),makeQuery(id+"F21.imprint","INTERSECT",VERTEX,{"derivedFrom":[subQ20,subQ18]}),makeQuery(id+"F21.imprint","INTERSECT",VERTEX,{"derivedFrom":[subQ18,subQ19]}),makeQuery(id+"F21.imprint","IMPRINT",EDGE,{"derivedFrom":subQ18}),makeQuery(id+"F22.imprint","INTERSECT",VERTEX,{"derivedFrom":[subQ17,subQ15]}),makeQuery(id+"F22.imprint","INTERSECT",VERTEX,{"derivedFrom":[subQ15,subQ16]}),makeQuery(id+"F22.imprint","IMPRINT",EDGE,{"derivedFrom":subQ15}),makeQuery(id+"F24.imprint","INTERSECT",VERTEX,{"derivedFrom":[subQ14,subQ12]}),makeQuery(id+"F24.imprint","INTERSECT",VERTEX,{"derivedFrom":[subQ12,subQ13]}),makeQuery(id+"F24.imprint","IMPRINT",EDGE,{"derivedFrom":subQ12}),makeQuery(id+"F26.imprint","INTERSECT",VERTEX,{"derivedFrom":[subQ11,subQ9]}),makeQuery(id+"F26.imprint","INTERSECT",VERTEX,{"derivedFrom":[subQ9,subQ10]}),makeQuery(id+"F26.imprint","IMPRINT",EDGE,{"derivedFrom":subQ9}),makeQuery(id+"F28.imprint","INTERSECT",VERTEX,{"derivedFrom":[subQ8,subQ6]}),makeQuery(id+"F28.imprint","INTERSECT",VERTEX,{"derivedFrom":[subQ6,subQ7]}),makeQuery(id+"F28.imprint","IMPRINT",EDGE,{"derivedFrom":subQ6}),makeQuery(id+"F30.imprint","INTERSECT",VERTEX,{"derivedFrom":[subQ5,subQ3]}),makeQuery(id+"F30.imprint","INTERSECT",VERTEX,{"derivedFrom":[subQ3,subQ4]}),makeQuery(id+"F30.imprint","IMPRINT",EDGE,{"derivedFrom":subQ3}),makeQuery(id+"F32.imprint","INTERSECT",VERTEX,{"derivedFrom":[subQ2,subQ0]}),makeQuery(id+"F32.imprint","INTERSECT",VERTEX,{"derivedFrom":[subQ0,subQ1]}),makeQuery(id+"F32.imprint","IMPRINT",EDGE,{"derivedFrom":subQ0})])]}),makeQuery(id+"F42.opExtrude","SWEPT_FACE",FACE,{"disambiguationData":[OSD([sQuery(id+"F41.wireOp",EDGE,"E63")])]})]});}
            var Q1;
            {var subQ0=sQuery(id+"F32.wireOp",EDGE,"E49");var subQ1=sQuery(id+"F32.wireOp",EDGE,"E50");var subQ2=sQuery(id+"F32.wireOp",EDGE,"E48");var subQ3=sQuery(id+"F30.wireOp",EDGE,"E46");var subQ4=sQuery(id+"F30.wireOp",EDGE,"E47");var subQ5=sQuery(id+"F30.wireOp",EDGE,"E45");var subQ6=sQuery(id+"F28.wireOp",EDGE,"E43");var subQ7=sQuery(id+"F28.wireOp",EDGE,"E44");var subQ8=sQuery(id+"F28.wireOp",EDGE,"E42");var subQ9=sQuery(id+"F26.wireOp",EDGE,"E40");var subQ10=sQuery(id+"F26.wireOp",EDGE,"E41");var subQ11=sQuery(id+"F26.wireOp",EDGE,"E39");var subQ12=sQuery(id+"F24.wireOp",EDGE,"E37");var subQ13=sQuery(id+"F24.wireOp",EDGE,"E38");var subQ14=sQuery(id+"F24.wireOp",EDGE,"E36");var subQ15=sQuery(id+"F22.wireOp",EDGE,"E34");var subQ16=sQuery(id+"F22.wireOp",EDGE,"E35");var subQ17=sQuery(id+"F22.wireOp",EDGE,"E33");var subQ18=sQuery(id+"F21.wireOp",EDGE,"E31");var subQ19=sQuery(id+"F21.wireOp",EDGE,"E32");var subQ20=sQuery(id+"F21.wireOp",EDGE,"E30");var subQ21=sQuery(id+"F19.wireOp",EDGE,"E28");var subQ22=sQuery(id+"F19.wireOp",EDGE,"E29");var subQ23=sQuery(id+"F19.wireOp",EDGE,"E27");var subQ24=sQuery(id+"F17.wireOp",EDGE,"E25");var subQ25=sQuery(id+"F17.wireOp",EDGE,"E26");var subQ26=sQuery(id+"F17.wireOp",EDGE,"E24");var subQ27=sQuery(id+"F15.wireOp",EDGE,"E22");var subQ28=sQuery(id+"F15.wireOp",EDGE,"E23");var subQ29=sQuery(id+"F15.wireOp",EDGE,"E21");var subQ30=sQuery(id+"F14.wireOp",EDGE,"E19");var subQ31=sQuery(id+"F14.wireOp",EDGE,"E20");var subQ32=sQuery(id+"F14.wireOp",EDGE,"E18");var subQ33=sQuery(id+"F13.wireOp",EDGE,"E16");var subQ34=sQuery(id+"F13.wireOp",EDGE,"E17");var subQ35=sQuery(id+"F13.wireOp",EDGE,"E15");var subQ36=sQuery(id+"F12.wireOp",EDGE,"E13");var subQ37=sQuery(id+"F12.wireOp",EDGE,"E14");var subQ38=sQuery(id+"F12.wireOp",EDGE,"E12");var subQ39=sQuery(id+"F11.wireOp",EDGE,"E10");var subQ40=sQuery(id+"F11.wireOp",EDGE,"E11");var subQ41=sQuery(id+"F11.wireOp",EDGE,"E9");var subQ42=sQuery(id+"F10.wireOp",EDGE,"E7");var subQ43=sQuery(id+"F10.wireOp",EDGE,"E8");var subQ44=sQuery(id+"F10.wireOp",EDGE,"E6");var subQ45=sQuery(id+"F9.wireOp",EDGE,"E4");var subQ46=sQuery(id+"F9.wireOp",EDGE,"E5");var subQ47=sQuery(id+"F9.wireOp",EDGE,"E3");var subQ48=sQuery(id+"F8.wireOp",EDGE,"E1");var subQ49=sQuery(id+"F8.wireOp",EDGE,"E2");var subQ50=sQuery(id+"F8.wireOp",EDGE,"E0");Q1=makeQuery(id+"F42.boolean.opBoolean","INTERSECT",EDGE,{"derivedFrom":[makeQuery(id+"F33.opLoft","SWEPT_FACE",FACE,{"disambiguationData":[OSD([subQ50,subQ48,subQ49,subQ47,subQ45,subQ46,subQ44,subQ42,subQ43,subQ41,subQ39,subQ40,subQ38,subQ36,subQ37,subQ35,subQ33,subQ34,subQ32,subQ30,subQ31,subQ29,subQ27,subQ28,subQ26,subQ24,subQ25,subQ23,subQ21,subQ22,subQ20,subQ18,subQ19,subQ17,subQ15,subQ16,subQ14,subQ12,subQ13,subQ11,subQ9,subQ10,subQ8,subQ6,subQ7,subQ5,subQ3,subQ4,subQ2,subQ0,subQ1]),TDD([makeQuery(id+"F8.imprint","INTERSECT",VERTEX,{"derivedFrom":[subQ50,subQ48]}),makeQuery(id+"F8.imprint","INTERSECT",VERTEX,{"derivedFrom":[subQ48,subQ49]}),makeQuery(id+"F8.imprint","IMPRINT",EDGE,{"derivedFrom":subQ48}),makeQuery(id+"F9.imprint","INTERSECT",VERTEX,{"derivedFrom":[subQ47,subQ45]}),makeQuery(id+"F9.imprint","INTERSECT",VERTEX,{"derivedFrom":[subQ45,subQ46]}),makeQuery(id+"F9.imprint","IMPRINT",EDGE,{"derivedFrom":subQ45}),makeQuery(id+"F10.imprint","INTERSECT",VERTEX,{"derivedFrom":[subQ44,subQ42]}),makeQuery(id+"F10.imprint","INTERSECT",VERTEX,{"derivedFrom":[subQ42,subQ43]}),makeQuery(id+"F10.imprint","IMPRINT",EDGE,{"derivedFrom":subQ42}),makeQuery(id+"F11.imprint","INTERSECT",VERTEX,{"derivedFrom":[subQ41,subQ39]}),makeQuery(id+"F11.imprint","INTERSECT",VERTEX,{"derivedFrom":[subQ39,subQ40]}),makeQuery(id+"F11.imprint","IMPRINT",EDGE,{"derivedFrom":subQ39}),makeQuery(id+"F12.imprint","INTERSECT",VERTEX,{"derivedFrom":[subQ38,subQ36]}),makeQuery(id+"F12.imprint","INTERSECT",VERTEX,{"derivedFrom":[subQ36,subQ37]}),makeQuery(id+"F12.imprint","IMPRINT",EDGE,{"derivedFrom":subQ36}),makeQuery(id+"F13.imprint","INTERSECT",VERTEX,{"derivedFrom":[subQ35,subQ33]}),makeQuery(id+"F13.imprint","INTERSECT",VERTEX,{"derivedFrom":[subQ33,subQ34]}),makeQuery(id+"F13.imprint","IMPRINT",EDGE,{"derivedFrom":subQ33}),makeQuery(id+"F14.imprint","INTERSECT",VERTEX,{"derivedFrom":[subQ32,subQ30]}),makeQuery(id+"F14.imprint","INTERSECT",VERTEX,{"derivedFrom":[subQ30,subQ31]}),makeQuery(id+"F14.imprint","IMPRINT",EDGE,{"derivedFrom":subQ30}),makeQuery(id+"F15.imprint","INTERSECT",VERTEX,{"derivedFrom":[subQ29,subQ27]}),makeQuery(id+"F15.imprint","INTERSECT",VERTEX,{"derivedFrom":[subQ27,subQ28]}),makeQuery(id+"F15.imprint","IMPRINT",EDGE,{"derivedFrom":subQ27}),makeQuery(id+"F17.imprint","INTERSECT",VERTEX,{"derivedFrom":[subQ26,subQ24]}),makeQuery(id+"F17.imprint","INTERSECT",VERTEX,{"derivedFrom":[subQ24,subQ25]}),makeQuery(id+"F17.imprint","IMPRINT",EDGE,{"derivedFrom":subQ24}),makeQuery(id+"F19.imprint","INTERSECT",VERTEX,{"derivedFrom":[subQ23,subQ21]}),makeQuery(id+"F19.imprint","INTERSECT",VERTEX,{"derivedFrom":[subQ21,subQ22]}),makeQuery(id+"F19.imprint","IMPRINT",EDGE,{"derivedFrom":subQ21}),makeQuery(id+"F21.imprint","INTERSECT",VERTEX,{"derivedFrom":[subQ20,subQ18]}),makeQuery(id+"F21.imprint","INTERSECT",VERTEX,{"derivedFrom":[subQ18,subQ19]}),makeQuery(id+"F21.imprint","IMPRINT",EDGE,{"derivedFrom":subQ18}),makeQuery(id+"F22.imprint","INTERSECT",VERTEX,{"derivedFrom":[subQ17,subQ15]}),makeQuery(id+"F22.imprint","INTERSECT",VERTEX,{"derivedFrom":[subQ15,subQ16]}),makeQuery(id+"F22.imprint","IMPRINT",EDGE,{"derivedFrom":subQ15}),makeQuery(id+"F24.imprint","INTERSECT",VERTEX,{"derivedFrom":[subQ14,subQ12]}),makeQuery(id+"F24.imprint","INTERSECT",VERTEX,{"derivedFrom":[subQ12,subQ13]}),makeQuery(id+"F24.imprint","IMPRINT",EDGE,{"derivedFrom":subQ12}),makeQuery(id+"F26.imprint","INTERSECT",VERTEX,{"derivedFrom":[subQ11,subQ9]}),makeQuery(id+"F26.imprint","INTERSECT",VERTEX,{"derivedFrom":[subQ9,subQ10]}),makeQuery(id+"F26.imprint","IMPRINT",EDGE,{"derivedFrom":subQ9}),makeQuery(id+"F28.imprint","INTERSECT",VERTEX,{"derivedFrom":[subQ8,subQ6]}),makeQuery(id+"F28.imprint","INTERSECT",VERTEX,{"derivedFrom":[subQ6,subQ7]}),makeQuery(id+"F28.imprint","IMPRINT",EDGE,{"derivedFrom":subQ6}),makeQuery(id+"F30.imprint","INTERSECT",VERTEX,{"derivedFrom":[subQ5,subQ3]}),makeQuery(id+"F30.imprint","INTERSECT",VERTEX,{"derivedFrom":[subQ3,subQ4]}),makeQuery(id+"F30.imprint","IMPRINT",EDGE,{"derivedFrom":subQ3}),makeQuery(id+"F32.imprint","INTERSECT",VERTEX,{"derivedFrom":[subQ2,subQ0]}),makeQuery(id+"F32.imprint","INTERSECT",VERTEX,{"derivedFrom":[subQ0,subQ1]}),makeQuery(id+"F32.imprint","IMPRINT",EDGE,{"derivedFrom":subQ0})])]}),makeQuery(id+"F42.opExtrude","SWEPT_FACE",FACE,{"disambiguationData":[OSD([sQuery(id+"F41.wireOp",EDGE,"E64")])]})]});}
            fillet(context, id + "F45", {"entities" : qUnion([Q0, Q1]), "radius" : 10 * mm, "tangentPropagation" : true, "allowEdgeOverflow" : false});
        }
        {
            var Q0;
            Q0=qCreatedBy(makeId("Front.planeOp"),FACE);
            var sketch = newSketch(context, id + "F46", { "sketchPlane" : qUnion([Q0])});
            skFitSpline(sketch, "E71", {"points": [v(-2091.53, 1174.7) * mm, v(-1998.7, 1143.42) * mm, v(-1883.42, 1133.14) * mm, v(-1836.6, 1134.28) * mm, v(-1828.23, 1128) * mm, v(-1840.8, 1110.9) * mm, v(-1887.48, 1099.02) * mm, v(-2002.3, 1122.34) * mm, v(-2091.53, 1174.7) * mm]});
            skSolve(sketch);
        }
        {
            var Q0;
            Q0=makeQuery(id+"FJKBhsVKbEwbYUU_1.opExtrude","CAP_FACE",FACE,{"disambiguationData":[OSD([sQuery(id+"F46.wireOp",EDGE,"E71")])],"isStart":false});
            var sketch = newSketch(context, id + "F47", { "sketchPlane" : qUnion([Q0])});
            skFitSpline(sketch, "E72", {"points": [v(1821.58, 1156.44) * mm, v(1819.39, 1082.1) * mm, v(1838.7, 1057.79) * mm, v(1965.38, 1066.7) * mm, v(2074.22, 1104.4) * mm, v(2106.53, 1140.86) * mm, v(2107.83, 1189.54) * mm, v(2077.32, 1193.44) * mm, v(1848.2, 1175.26) * mm]});
            skSolve(sketch);
        }
        {
            var Q0;
            Q0=qCreatedBy(makeId("Front.planeOp"),FACE);
            cPlane(context, id + "F48", {"entities" : qUnion([Q0]), "cplaneType" : CPlaneType.OFFSET, "offset" : 550 * mm, "oppositeDirection" : true, "width" : 150 * mm, "height" : 150 * mm});
        }
        {
            var Q0;
            Q0=qCreatedBy(id+"F48.planeOp",FACE);
            var sketch = newSketch(context, id + "F49", { "sketchPlane" : qUnion([Q0])});
            skLineSegment(sketch, "E73", {"start": v(-1934.78, 1118.14) * mm, "end": v(-1796.74, 913.58) * mm});
            skLineSegment(sketch, "E74", {"start": v(-1796.74, 913.58) * mm, "end": v(-1923.88, 910.37) * mm});
            skLineSegment(sketch, "E75", {"start": v(-1923.88, 910.37) * mm, "end": v(-2067.86, 1160.25) * mm});
            skLineSegment(sketch, "E76", {"start": v(-2067.86, 1160.25) * mm, "end": v(-1934.78, 1118.14) * mm});
            skSolve(sketch);
        }
        {
            var Q0;
            Q0=qCreatedBy(makeId("Front.planeOp"),FACE);
            var sketch = newSketch(context, id + "F50", { "sketchPlane" : qUnion([Q0])});
            skFitSpline(sketch, "E77", {"points": [v(-1916.26, 902.4) * mm, v(-1961.26, 913.9) * mm, v(-2001.08, 926.2) * mm, v(-2032.34, 936.61) * mm, v(-2082.2, 954.66) * mm, v(-2086.3, 954.85) * mm, v(-2084.38, 948.95) * mm, v(-2076.34, 935.13) * mm, v(-2071.96, 920.11) * mm, v(-2070.7, 902.28) * mm], "startDerivative": vector(-347.74, 101.24) * mm, "endDerivative": vector(0, -334.42) * mm});
            skLineSegment(sketch, "E78", {"start": v(-2070.7, 902.28) * mm, "end": v(-1916.26, 902.4) * mm});
            skSolve(sketch);
        }
        {
            var Q0;
            Q0 = qSketchRegion(id + "F50", true);
            extrude(context, id + "F51", {"entities" : qUnion([Q0]), "operationType" : NewBodyOperationType.ADD, "oppositeDirection" : true, "depth" : 600 * mm, "offsetDistance" : 25 * mm});
        }
        {
            var Q0;
            Q0=makeQuery(id+"F33.opLoft","SWEPT_BODY",BODY,{"disambiguationData":[OSD([sQuery(id+"F8.wireOp",EDGE,"E0"),sQuery(id+"F9.wireOp",EDGE,"E3"),sQuery(id+"F10.wireOp",EDGE,"E6"),sQuery(id+"F11.wireOp",EDGE,"E9"),sQuery(id+"F12.wireOp",EDGE,"E12"),sQuery(id+"F13.wireOp",EDGE,"E15"),sQuery(id+"F14.wireOp",EDGE,"E18"),sQuery(id+"F15.wireOp",EDGE,"E21"),sQuery(id+"F17.wireOp",EDGE,"E24"),sQuery(id+"F19.wireOp",EDGE,"E27"),makeQuery(id+"F21.imprint","IMPRINT",FACE,{"disambiguationData":[TD([[makeQuery(id+"F21.imprint","IMPRINT",EDGE,{"derivedFrom":sQuery(id+"F21.wireOp",EDGE,"E30")}),1.0]])]}),sQuery(id+"F22.wireOp",EDGE,"E33"),sQuery(id+"F24.wireOp",EDGE,"E36"),sQuery(id+"F26.wireOp",EDGE,"E39"),sQuery(id+"F28.wireOp",EDGE,"E42"),makeQuery(id+"F30.imprint","IMPRINT",FACE,{"disambiguationData":[TD([[makeQuery(id+"F30.imprint","IMPRINT",EDGE,{"derivedFrom":sQuery(id+"F30.wireOp",EDGE,"E45")}),1.0]])]}),sQuery(id+"F32.wireOp",EDGE,"E48")])]});
            var Q1;
            Q1=qCreatedBy(makeId("Front.planeOp"),FACE);
            mirror(context, id + "F52", {"operationType" : NewBodyOperationType.ADD, "entities" : qUnion([Q0]), "mirrorPlane" : qUnion([Q1])});
        }
    });
